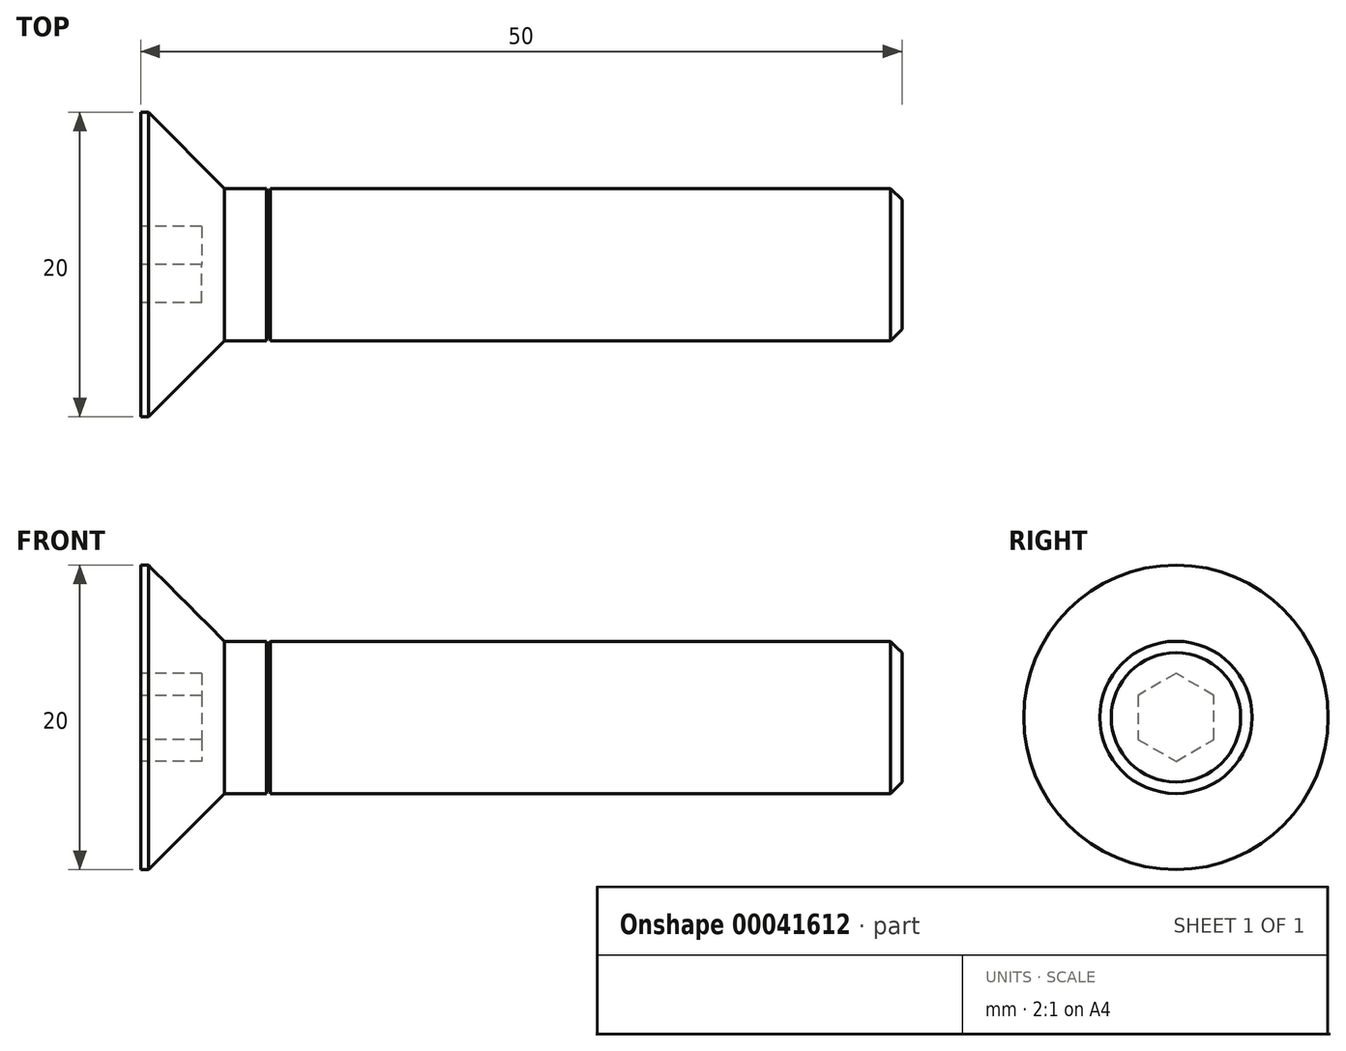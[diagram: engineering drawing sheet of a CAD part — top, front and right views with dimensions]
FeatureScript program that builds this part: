
annotation { "Feature Type Name" : "Feature", "Feature Type Description" : "" }
export const myFeature = defineFeature(function(context is Context, id is Id, definition is map)
    precondition{}
    {
        {
            var Q0;
            Q0=qCreatedBy(makeId("Front.planeOp"),FACE);
            var sketch = newSketch(context, id + "F0", { "sketchPlane" : qUnion([Q0])});
            skLineSegment(sketch, "E0.rect.bottom", {"start": v(5.5, 10) * mm, "end": v(0, 10) * mm});
            skLineSegment(sketch, "E0.rect.top", {"start": v(50, -10) * mm, "end": v(0, -10) * mm, "construction": true});
            skLineSegment(sketch, "E0.rect.left", {"start": v(50, 10) * mm, "end": v(50, -10) * mm, "construction": true});
            skLineSegment(sketch, "E0.rect.right", {"start": v(0, 10) * mm, "end": v(0, -10) * mm, "construction": true});
            skPoint(sketch, "E0.rect.middle", {"position": v(25, 0) * mm});
            skLineSegment(sketch, "E1", {"start": v(0, 0) * mm, "end": v(50, 0) * mm});
            skLineSegment(sketch, "E2", {"start": v(0, 10) * mm, "end": v(0, 0) * mm});
            skLineSegment(sketch, "E3", {"start": v(50, 4.25) * mm, "end": v(50, 0) * mm});
            skLineSegment(sketch, "E4", {"start": v(5.5, 10) * mm, "end": v(5.5, 5) * mm});
            skLineSegment(sketch, "E5", {"start": v(5.5, 5) * mm, "end": v(8.25, 5) * mm});
            skLineSegment(sketch, "E6", {"start": v(8.25, 5) * mm, "end": v(8.38, 4.25) * mm});
            skLineSegment(sketch, "E7", {"start": v(8.38, 4.25) * mm, "end": v(8.5, 5) * mm});
            skLineSegment(sketch, "E8", {"start": v(8.5, 5) * mm, "end": v(49.25, 5) * mm});
            skLineSegment(sketch, "E9", {"start": v(49.25, 5) * mm, "end": v(50, 4.25) * mm});
            skLineSegment(sketch, "E10", {"start": v(8.38, 4.25) * mm, "end": v(50, 4.25) * mm, "construction": true});
            skLineSegment(sketch, "E11", {"start": v(49.25, 5) * mm, "end": v(50, 5.75) * mm, "construction": true});
            skPoint(sketch, "E12", {"position": v(50, 4.25) * mm});
            skPoint(sketch, "E13", {"position": v(49.25, 5) * mm});
            skPoint(sketch, "E14", {"position": v(50, -4.25) * mm});
            skLineSegment(sketch, "E15", {"start": v(50, 0) * mm, "end": v(50, -4.25) * mm});
            skLineSegment(sketch, "E16", {"start": v(49.25, 5) * mm, "end": v(49.25, -5) * mm, "construction": true});
            skPoint(sketch, "E17", {"position": v(49.25, 0) * mm});
            skSolve(sketch);
        }
        {
            var Q0;
            Q0=makeQuery(id+"F0.imprint","IMPRINT",FACE,{"disambiguationData":[TD([[makeQuery(id+"F0.imprint","IMPRINT",EDGE,{"derivedFrom":sQuery(id+"F0.wireOp",EDGE,"E0.rect.bottom")}),1.0]])]});
            var Q1;
            Q1=sQuery(id+"F0.wireOp",EDGE,"E1");
            revolve(context, id + "F1", {"entities" : qUnion([Q0]), "axis" : qUnion([Q1]), "revolveType" : RevolveType.FULL});
        }
        {
            var Q0;
            Q0=makeQuery(id+"F1.opRevolve","SWEPT_FACE",FACE,{"disambiguationData":[OSD([sQuery(id+"F0.wireOp",EDGE,"E2")])]});
            var sketch = newSketch(context, id + "F2", { "sketchPlane" : qUnion([Q0])});
            skCircle(sketch, "E18.cCircle", {"center": v(0, 0) * mm, "radius": 2.89 * mm, "construction": true});
            skLineSegment(sketch, "E18.0", {"start": v(2.5, -1.44) * mm, "end": v(0, -2.89) * mm});
            skLineSegment(sketch, "E18.1", {"start": v(0, -2.89) * mm, "end": v(-2.5, -1.44) * mm});
            skLineSegment(sketch, "E18.2", {"start": v(-2.5, -1.44) * mm, "end": v(-2.5, 1.44) * mm});
            skLineSegment(sketch, "E18.3", {"start": v(-2.5, 1.44) * mm, "end": v(0, 2.89) * mm});
            skLineSegment(sketch, "E18.4", {"start": v(0, 2.89) * mm, "end": v(2.5, 1.44) * mm});
            skLineSegment(sketch, "E18.5", {"start": v(2.5, 1.44) * mm, "end": v(2.5, -1.44) * mm});
            skCircle(sketch, "E19.0", {"center": v(0, 0) * mm, "radius": 10 * mm});
            skSolve(sketch);
        }
        {
            var Q0;
            Q0=makeQuery(id+"F2.imprint","IMPRINT",FACE,{"disambiguationData":[TD([[makeQuery(id+"F2.imprint","IMPRINT",EDGE,{"derivedFrom":sQuery(id+"F2.wireOp",EDGE,"E18.0")}),-1.0]])]});
            extrude(context, id + "F3", {"entities" : qUnion([Q0]), "operationType" : NewBodyOperationType.REMOVE, "oppositeDirection" : true, "depth" : 4 * mm});
        }
        {
            var Q0;
            Q0=makeQuery(id+"F1.opRevolve","SWEPT_EDGE",EDGE,{"disambiguationData":[OSD([sQuery(id+"F0.wireOp",EDGE,"E0.rect.bottom"),sQuery(id+"F0.wireOp",EDGE,"E4")])]});
            chamfer(context, id + "F4", {"entities" : qUnion([Q0]), "width" : 5 * mm, "tangentPropagation" : true});
        }
    });
